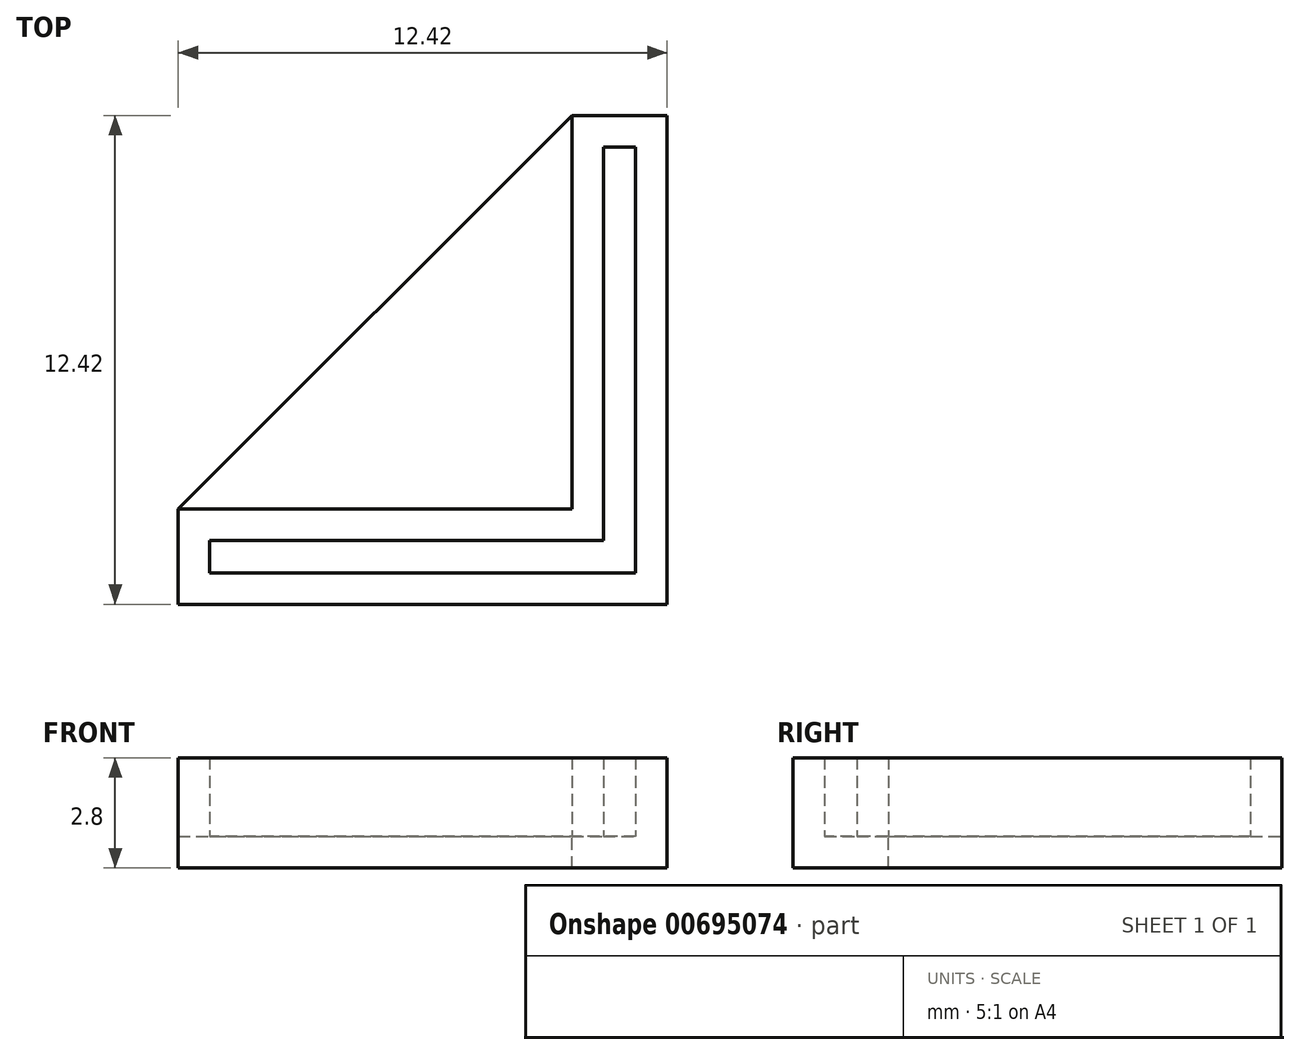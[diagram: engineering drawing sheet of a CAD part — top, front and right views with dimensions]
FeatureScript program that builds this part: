
annotation { "Feature Type Name" : "Feature", "Feature Type Description" : "" }
export const myFeature = defineFeature(function(context is Context, id is Id, definition is map)
    precondition{}
    {
        {
            var Q0;
            Q0=qCreatedBy(makeId("Top.planeOp"),FACE);
            var sketch = newSketch(context, id + "F0", { "sketchPlane" : qUnion([Q0])});
            skLineSegment(sketch, "E0", {"start": v(-0.4, 0.4) * mm, "end": v(-0.4, 10.4) * mm});
            skLineSegment(sketch, "E1", {"start": v(-0.4, 10.4) * mm, "end": v(0.4, 10.4) * mm});
            skLineSegment(sketch, "E2", {"start": v(0.4, 10.4) * mm, "end": v(0.41, 0.41) * mm});
            skLineSegment(sketch, "E3", {"start": v(0.4, 0.4) * mm, "end": v(10.4, 0.41) * mm});
            skLineSegment(sketch, "E4", {"start": v(10.4, 0.4) * mm, "end": v(10.4, -0.4) * mm});
            skLineSegment(sketch, "E5", {"start": v(10.4, -0.4) * mm, "end": v(0.4, -0.41) * mm});
            skLineSegment(sketch, "E6", {"start": v(0.41, -0.4) * mm, "end": v(0.41, -10.4) * mm});
            skLineSegment(sketch, "E7", {"start": v(0.4, -10.4) * mm, "end": v(-0.4, -10.4) * mm});
            skLineSegment(sketch, "E8", {"start": v(-0.4, -10.4) * mm, "end": v(-0.4, -0.4) * mm});
            skLineSegment(sketch, "E9", {"start": v(-0.4, -0.4) * mm, "end": v(-10.4, -0.4) * mm});
            skLineSegment(sketch, "E10", {"start": v(-10.4, -0.4) * mm, "end": v(-10.4, 0.4) * mm});
            skLineSegment(sketch, "E11", {"start": v(-10.4, 0.4) * mm, "end": v(-0.4, 0.4) * mm});
            skPoint(sketch, "E12", {"position": v(0, 10.4) * mm});
            skPoint(sketch, "E13", {"position": v(-10.4, 0) * mm});
            skLineSegment(sketch, "E14.0", {"start": v(-11.21, -1.21) * mm, "end": v(-11.21, 1.21) * mm});
            skLineSegment(sketch, "E14.1", {"start": v(1.21, 1.2) * mm, "end": v(11.21, 1.21) * mm});
            skLineSegment(sketch, "E14.2", {"start": v(1.2, 11.2) * mm, "end": v(1.21, 1.21) * mm});
            skLineSegment(sketch, "E14.3", {"start": v(-1.21, 11.2) * mm, "end": v(1.21, 11.2) * mm});
            skLineSegment(sketch, "E14.4", {"start": v(-1.21, 1.21) * mm, "end": v(-1.21, 11.2) * mm});
            skLineSegment(sketch, "E14.5", {"start": v(11.21, 1.21) * mm, "end": v(11.21, -1.21) * mm});
            skLineSegment(sketch, "E14.6", {"start": v(-11.21, 1.21) * mm, "end": v(-1.21, 1.21) * mm});
            skLineSegment(sketch, "E14.7", {"start": v(11.21, -1.2) * mm, "end": v(1.21, -1.21) * mm});
            skLineSegment(sketch, "E14.8", {"start": v(1.21, -1.21) * mm, "end": v(1.21, -11.2) * mm});
            skLineSegment(sketch, "E14.9", {"start": v(1.21, -11.2) * mm, "end": v(-1.21, -11.2) * mm});
            skLineSegment(sketch, "E14.10", {"start": v(-1.21, -11.2) * mm, "end": v(-1.21, -1.21) * mm});
            skLineSegment(sketch, "E14.11", {"start": v(-1.21, -1.21) * mm, "end": v(-11.21, -1.21) * mm});
            skLineSegment(sketch, "E15", {"start": v(-11.21, 1.2) * mm, "end": v(-1.2, 11.2) * mm});
            skLineSegment(sketch, "E16", {"start": v(1.2, 11.2) * mm, "end": v(11.21, 1.2) * mm});
            skLineSegment(sketch, "E17", {"start": v(11.21, -1.2) * mm, "end": v(1.2, -11.2) * mm});
            skLineSegment(sketch, "E18", {"start": v(-1.2, -11.2) * mm, "end": v(-11.21, -1.21) * mm});
            skLineSegment(sketch, "E19", {"start": v(-1.21, -1.21) * mm, "end": v(1.21, -1.21) * mm});
            skLineSegment(sketch, "E20", {"start": v(-0.4, -0.4) * mm, "end": v(0.4, -0.41) * mm});
            skLineSegment(sketch, "E21", {"start": v(1.21, 1.2) * mm, "end": v(1.21, -1.21) * mm});
            skLineSegment(sketch, "E22", {"start": v(0.4, -0.41) * mm, "end": v(0.41, 0.41) * mm});
            skSolve(sketch);
        }
        {
            var Q0;
            Q0=makeQuery(id+"F0.imprint","IMPRINT",FACE,{"disambiguationData":[TD([[makeQuery(id+"F0.imprint","IMPRINT",EDGE,{"derivedFrom":sQuery(id+"F0.wireOp",EDGE,"E0")}),1.0]])]});
            var Q1;
            {var subQ0=sQuery(id+"F0.wireOp",EDGE,"E20");Q1=makeQuery(id+"F0.imprint","IMPRINT",FACE,{"disambiguationData":[TD([[makeQuery(id+"F0.imprint","IMPRINT",EDGE,{"derivedFrom":subQ0}),-1.0]])]});}
            var Q2;
            {var subQ0=sQuery(id+"F0.wireOp",EDGE,"E22");Q2=makeQuery(id+"F0.imprint","IMPRINT",FACE,{"disambiguationData":[TD([[makeQuery(id+"F0.imprint","IMPRINT",EDGE,{"derivedFrom":subQ0}),-1.0]])]});}
            var Q3;
            {var subQ1=sQuery(id+"F0.wireOp",EDGE,"E5");var subQ3=sQuery(id+"F0.wireOp",EDGE,"E21");var subQ4=makeQuery(id+"F0.imprint","INTERSECT",VERTEX,{"derivedFrom":[subQ1,subQ3]});Q3=makeQuery(id+"F0.imprint","IMPRINT",FACE,{"disambiguationData":[TD([[makeQuery(id+"F0.imprint","IMPRINT",EDGE,{"disambiguationData":[TD([[subQ4,-1.0]])],"derivedFrom":subQ1}),1.0]])]});}
            extrude(context, id + "F1", {"entities" : qUnion([Q0, Q1, Q2, Q3]), "depth" : 2 * mm, "offsetDistance" : 25 * mm});
        }
        {
            var Q0;
            Q0=makeQuery(id+"F0.imprint","IMPRINT",FACE,{"disambiguationData":[TD([[makeQuery(id+"F0.imprint","IMPRINT",EDGE,{"derivedFrom":sQuery(id+"F0.wireOp",EDGE,"E14.4")}),1.0]])]});
            var Q1;
            Q1=makeQuery(id+"F0.imprint","IMPRINT",FACE,{"disambiguationData":[TD([[makeQuery(id+"F0.imprint","IMPRINT",EDGE,{"derivedFrom":sQuery(id+"F0.wireOp",EDGE,"E0")}),1.0]])]});
            var Q2;
            Q2=makeQuery(id+"F1.opExtrude","CAP_FACE",FACE,{"disambiguationData":[OSD([sQuery(id+"F0.wireOp",EDGE,"E0"),sQuery(id+"F0.wireOp",EDGE,"E1"),sQuery(id+"F0.wireOp",EDGE,"E2"),sQuery(id+"F0.wireOp",EDGE,"E3"),sQuery(id+"F0.wireOp",EDGE,"E4"),sQuery(id+"F0.wireOp",EDGE,"E5"),sQuery(id+"F0.wireOp",EDGE,"E6"),sQuery(id+"F0.wireOp",EDGE,"E7"),sQuery(id+"F0.wireOp",EDGE,"E8"),sQuery(id+"F0.wireOp",EDGE,"E9"),sQuery(id+"F0.wireOp",EDGE,"E10"),sQuery(id+"F0.wireOp",EDGE,"E11")])],"isStart":false});
            var Q3;
            Q3=makeQuery(id+"F0.imprint","IMPRINT",FACE,{"disambiguationData":[TD([[makeQuery(id+"F0.imprint","IMPRINT",EDGE,{"derivedFrom":sQuery(id+"F0.wireOp",EDGE,"E0")}),-1.0]])]});
            var Q4;
            {var subQ0=sQuery(id+"F0.wireOp",EDGE,"E20");Q4=makeQuery(id+"F0.imprint","IMPRINT",FACE,{"disambiguationData":[TD([[makeQuery(id+"F0.imprint","IMPRINT",EDGE,{"derivedFrom":subQ0}),-1.0]])]});}
            var Q5;
            {var subQ0=sQuery(id+"F0.wireOp",EDGE,"E22");Q5=makeQuery(id+"F0.imprint","IMPRINT",FACE,{"disambiguationData":[TD([[makeQuery(id+"F0.imprint","IMPRINT",EDGE,{"derivedFrom":subQ0}),-1.0]])]});}
            var Q6;
            {var subQ1=sQuery(id+"F0.wireOp",EDGE,"E5");var subQ3=sQuery(id+"F0.wireOp",EDGE,"E21");var subQ4=makeQuery(id+"F0.imprint","INTERSECT",VERTEX,{"derivedFrom":[subQ1,subQ3]});Q6=makeQuery(id+"F0.imprint","IMPRINT",FACE,{"disambiguationData":[TD([[makeQuery(id+"F0.imprint","IMPRINT",EDGE,{"disambiguationData":[TD([[subQ4,-1.0]])],"derivedFrom":subQ1}),1.0]])]});}
            extrude(context, id + "F2", {"entities" : qUnion([Q0, Q1, Q2, Q3, Q4, Q5, Q6]), "operationType" : NewBodyOperationType.ADD, "oppositeDirection" : true, "depth" : 0.8 * mm, "offsetDistance" : 25 * mm});
        }
    });
